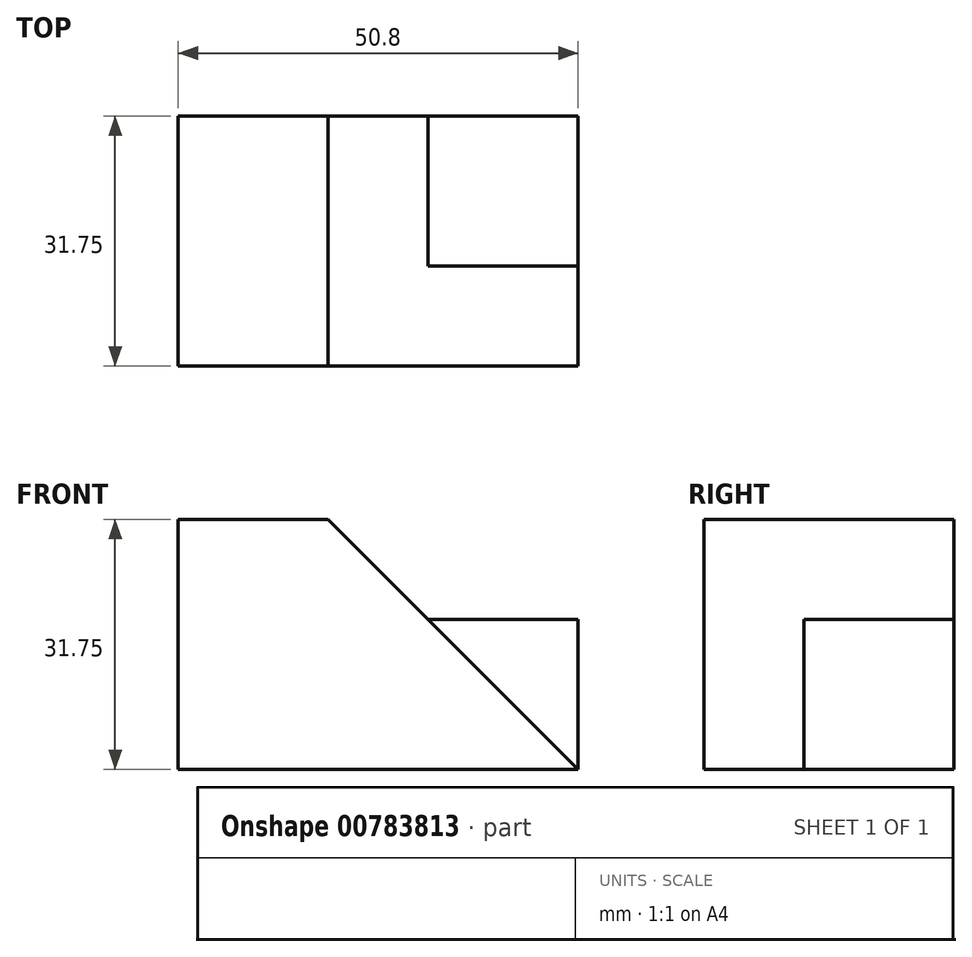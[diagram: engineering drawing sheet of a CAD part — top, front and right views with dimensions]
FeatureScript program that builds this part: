
annotation { "Feature Type Name" : "Feature", "Feature Type Description" : "" }
export const myFeature = defineFeature(function(context is Context, id is Id, definition is map)
    precondition{}
    {
        {
            var Q0;
            Q0=qCreatedBy(makeId("Front.planeOp"),FACE);
            var sketch = newSketch(context, id + "F0", { "sketchPlane" : qUnion([Q0])});
            skLineSegment(sketch, "E0", {"start": v(0, 0) * mm, "end": v(0, -31.75) * mm});
            skPoint(sketch, "E1.endSnap0", {"position": v(0, -15.88) * mm});
            skLineSegment(sketch, "E2", {"start": v(0, -31.75) * mm, "end": v(50.8, -31.75) * mm});
            skLineSegment(sketch, "E3", {"start": v(50.8, -31.75) * mm, "end": v(50.8, 0) * mm});
            skLineSegment(sketch, "E4", {"start": v(50.8, 0) * mm, "end": v(0, 0) * mm});
            skSolve(sketch);
        }
        {
            var Q0;
            Q0 = qSketchRegion(id + "F0", true);
            extrude(context, id + "F1", {"entities" : qUnion([Q0]), "depth" : 31.75 * mm, "offsetDistance" : 25.4 * mm});
        }
        {
            var Q0;
            Q0=makeQuery(id+"F1.opExtrude","SWEPT_FACE",FACE,{"disambiguationData":[OSD([sQuery(id+"F0.wireOp",EDGE,"E3")])]});
            var sketch = newSketch(context, id + "F2", { "sketchPlane" : qUnion([Q0])});
            skLineSegment(sketch, "E5", {"start": v(-19.05, -12.7) * mm, "end": v(0, -12.7) * mm});
            skLineSegment(sketch, "E6", {"start": v(-19.05, -12.7) * mm, "end": v(-19.05, -31.75) * mm});
            skSolve(sketch);
        }
        {
            var Q0;
            Q0=makeQuery(id+"F1.opExtrude","CAP_FACE",FACE,{"disambiguationData":[OSD([sQuery(id+"F0.wireOp",EDGE,"E0"),sQuery(id+"F0.wireOp",EDGE,"E2"),sQuery(id+"F0.wireOp",EDGE,"E3"),sQuery(id+"F0.wireOp",EDGE,"E4")])],"isStart":false});
            var sketch = newSketch(context, id + "F3", { "sketchPlane" : qUnion([Q0])});
            skLineSegment(sketch, "E7", {"start": v(0, 0) * mm, "end": v(19.05, 0) * mm});
            skLineSegment(sketch, "E8", {"start": v(19.05, 0) * mm, "end": v(50.8, -31.75) * mm});
            skSolve(sketch);
        }
        {
            var Q0;
            Q0 = qSketchRegion(id + "F3", true);
            var Q1;
            {var subQ0=sQuery(id+"F3.wireOp",EDGE,"E8");Q1=makeQuery(id+"F3.imprint","IMPRINT",FACE,{"disambiguationData":[TD([[makeQuery(id+"F3.imprint","IMPRINT",EDGE,{"derivedFrom":subQ0}),1.0]])]});}
            extrude(context, id + "F4", {"entities" : qUnion([Q0, Q1]), "operationType" : NewBodyOperationType.REMOVE, "oppositeDirection" : true, "depth" : 31.75 * mm, "offsetDistance" : 25.4 * mm});
        }
        {
            var Q0;
            {var subQ0=sQuery(id+"F2.wireOp",EDGE,"E5");Q0=makeQuery(id+"F2.imprint","IMPRINT",FACE,{"disambiguationData":[TD([[makeQuery(id+"F2.imprint","IMPRINT",EDGE,{"derivedFrom":subQ0}),-1.0]])]});}
            extrude(context, id + "F5", {"entities" : qUnion([Q0]), "operationType" : NewBodyOperationType.ADD, "oppositeDirection" : true, "depth" : 25.4 * mm, "offsetDistance" : 25.4 * mm});
        }
    });
